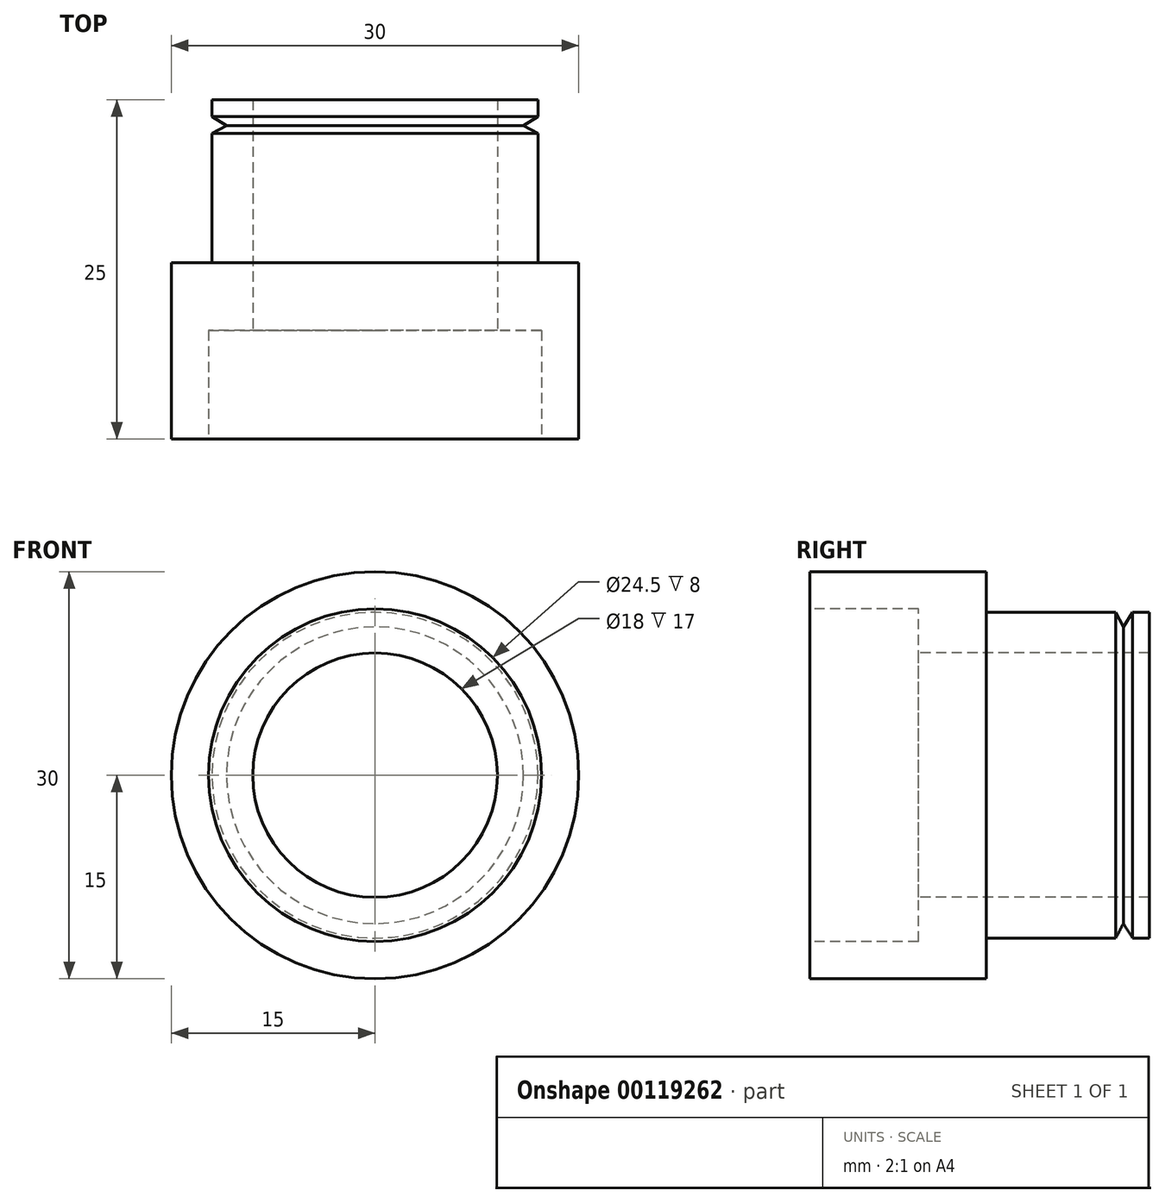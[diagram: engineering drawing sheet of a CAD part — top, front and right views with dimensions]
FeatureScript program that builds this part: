
annotation { "Feature Type Name" : "Feature", "Feature Type Description" : "" }
export const myFeature = defineFeature(function(context is Context, id is Id, definition is map)
    precondition{}
    {
        {
            var Q0;
            Q0=qCreatedBy(makeId("Right.planeOp"),FACE);
            var sketch = newSketch(context, id + "F0", { "sketchPlane" : qUnion([Q0])});
            skLineSegment(sketch, "E0", {"start": v(0, 0) * mm, "end": v(48.61, 0) * mm});
            skLineSegment(sketch, "E1", {"start": v(0, 12.25) * mm, "end": v(8, 12.25) * mm});
            skLineSegment(sketch, "E2", {"start": v(8, 12.25) * mm, "end": v(8, 9) * mm});
            skLineSegment(sketch, "E3", {"start": v(8, 9) * mm, "end": v(25, 9) * mm});
            skLineSegment(sketch, "E4", {"start": v(25, 9) * mm, "end": v(25, 12) * mm});
            skLineSegment(sketch, "E5", {"start": v(25, 12) * mm, "end": v(23.77, 12) * mm});
            skLineSegment(sketch, "E6", {"start": v(23.77, 12) * mm, "end": v(23.1, 10.93) * mm});
            skLineSegment(sketch, "E7", {"start": v(22.53, 12) * mm, "end": v(23.1, 10.93) * mm});
            skLineSegment(sketch, "E8", {"start": v(22.53, 12) * mm, "end": v(13, 12) * mm});
            skLineSegment(sketch, "E9", {"start": v(0, 15) * mm, "end": v(0, 12.25) * mm});
            skLineSegment(sketch, "E10", {"start": v(13, 12) * mm, "end": v(13, 15) * mm});
            skLineSegment(sketch, "E11.trimOffspring", {"start": v(13, 15) * mm, "end": v(0, 15) * mm});
            skSolve(sketch);
        }
        {
            var Q0;
            Q0=makeQuery(id+"F0.imprint","IMPRINT",FACE,{"disambiguationData":[TD([[makeQuery(id+"F0.imprint","IMPRINT",EDGE,{"derivedFrom":sQuery(id+"F0.wireOp",EDGE,"E1")}),1.0]])]});
            var Q1;
            Q1=sQuery(id+"F0.wireOp",EDGE,"E0");
            revolve(context, id + "F1", {"entities" : qUnion([Q0]), "axis" : qUnion([Q1]), "revolveType" : RevolveType.FULL});
        }
    });
